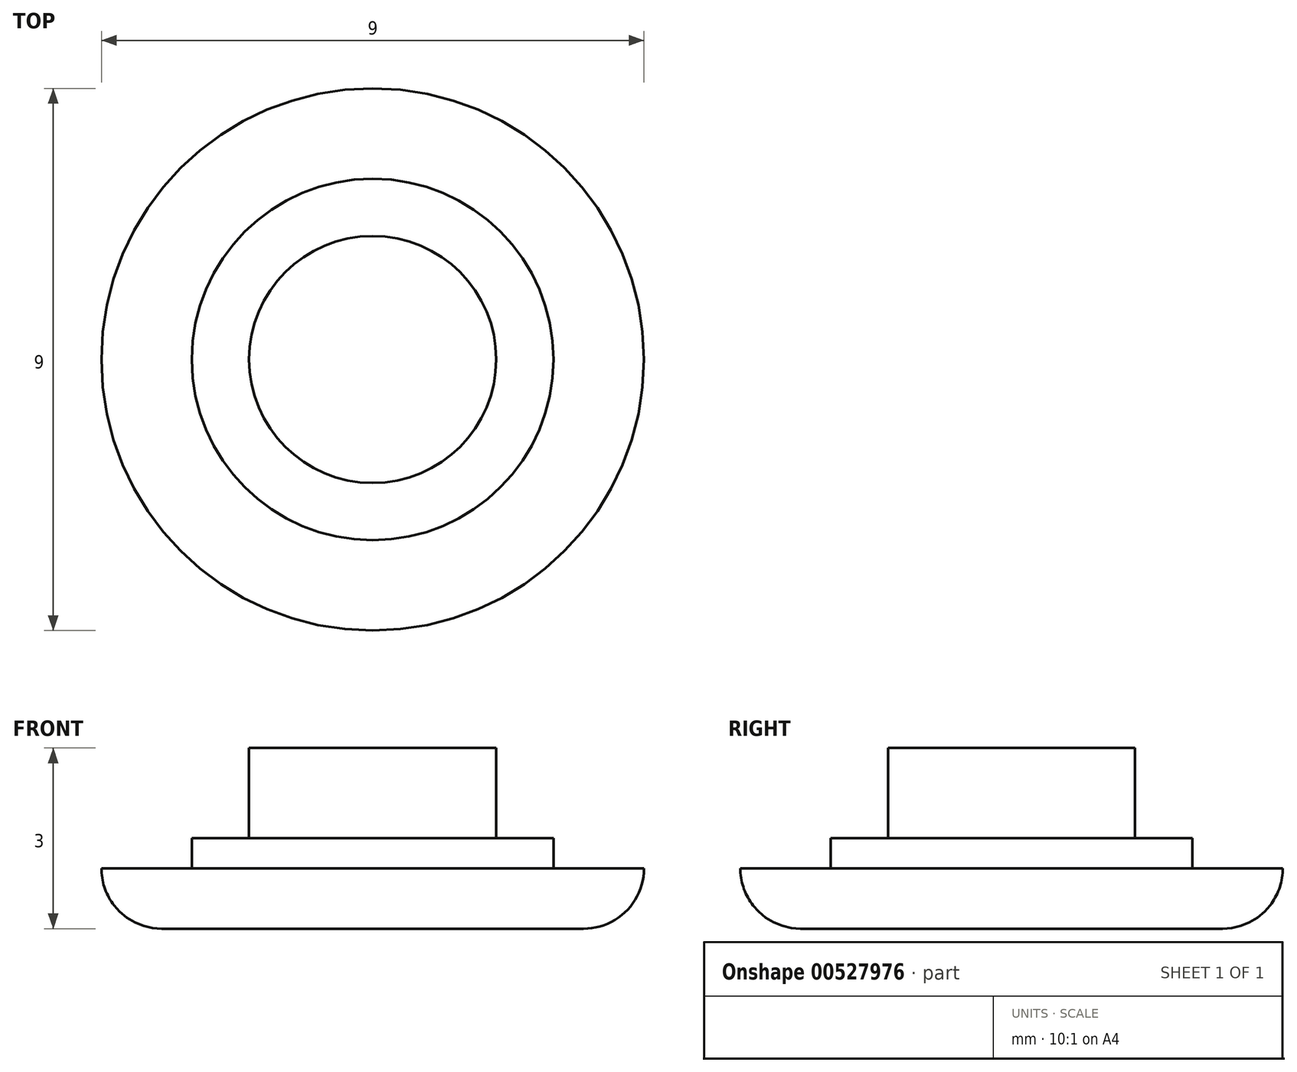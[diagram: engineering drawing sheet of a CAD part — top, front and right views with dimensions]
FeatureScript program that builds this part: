
annotation { "Feature Type Name" : "Feature", "Feature Type Description" : "" }
export const myFeature = defineFeature(function(context is Context, id is Id, definition is map)
    precondition{}
    {
        {
            var Q0;
            Q0=qCreatedBy(makeId("Top.planeOp"),FACE);
            var sketch = newSketch(context, id + "F0", { "sketchPlane" : qUnion([Q0])});
            skCircle(sketch, "E0", {"center": v(0, 0) * mm, "radius": 4.5 * mm});
            skSolve(sketch);
        }
        {
            var Q0;
            Q0=makeQuery(id+"F0.imprint","IMPRINT",FACE,{"disambiguationData":[TD([[makeQuery(id+"F0.imprint","IMPRINT",EDGE,{"derivedFrom":sQuery(id+"F0.wireOp",EDGE,"E0")}),1.0]])]});
            extrude(context, id + "F1", {"entities" : qUnion([Q0]), "depth" : 1 * mm, "offsetDistance" : 25 * mm});
        }
        {
            var Q0;
            Q0=makeQuery(id+"F1.opExtrude","CAP_FACE",FACE,{"disambiguationData":[OSD([sQuery(id+"F0.wireOp",EDGE,"E0")])],"isStart":false});
            var sketch = newSketch(context, id + "F2", { "sketchPlane" : qUnion([Q0])});
            skCircle(sketch, "E1", {"center": v(0, 0) * mm, "radius": 3 * mm});
            skSolve(sketch);
        }
        {
            var Q0;
            Q0=makeQuery(id+"F2.imprint","IMPRINT",FACE,{"disambiguationData":[TD([[makeQuery(id+"F2.imprint","IMPRINT",EDGE,{"derivedFrom":sQuery(id+"F2.wireOp",EDGE,"E1")}),1.0]])]});
            extrude(context, id + "F3", {"entities" : qUnion([Q0]), "operationType" : NewBodyOperationType.ADD, "depth" : .5 * mm, "offsetDistance" : 25 * mm});
        }
        {
            var Q0;
            Q0=makeQuery(id+"F3.opExtrude","CAP_FACE",FACE,{"disambiguationData":[OSD([sQuery(id+"F2.wireOp",EDGE,"E1")])],"isStart":false});
            var sketch = newSketch(context, id + "F4", { "sketchPlane" : qUnion([Q0])});
            skCircle(sketch, "E2", {"center": v(0, 0) * mm, "radius": 2.05 * mm});
            skSolve(sketch);
        }
        {
            var Q0;
            Q0=qSketchRegion(id+"F4",true);
            extrude(context, id + "F5", {"entities" : qUnion([Q0]), "operationType" : NewBodyOperationType.ADD, "depth" : 1.5 * mm, "offsetDistance" : 25 * mm});
        }
        {
            var Q0;
            Q0=makeQuery(id+"F1.opExtrude","CAP_EDGE",EDGE,{"disambiguationData":[OSD([sQuery(id+"F0.wireOp",EDGE,"E0")])],"isStart":true});
            fillet(context, id + "F6", {"entities" : qUnion([Q0]), "radius" : 1 * mm, "tangentPropagation" : true, "allowEdgeOverflow" : false});
        }
    });
